# Revit family: Maxlogic Panneau de contrôle d'extinction, 4 zone de détection, 1 zone d'extinction
name_source: partatom
category: Fire Alarm Devices
units: mm (PartAtom-declared; Revit-internal decimal feet)

## family parameters
Cut with Voids When Loaded = No
Host = Face
Maintain Annotation Orientation = Yes
OmniClass Number = 23.85.30.21
OmniClass Title = Environmental Detection/Registration
Part Type = Normal
Room Calculation Point = No
Round Connector Dimension = Use Diameter
Shared = No

## types (1)
- Panneau de Contrôle d'Extinction, 4 zone de détection, 1 sortie zone d'extinction
    Adresse ligne 1 = Şerifali Mahallesi Kutup Sokak No:27/1-2-4 Ümraniye TR-34775 İSTANBUL
    Alimentation d'externe = 220 V AC
    Batterie = 2 X (12V DC 7 Ah )
    Code de  Performance = EN 54-2, EN 54-4
    Code de Produit = ML-322
    Cost = 0 $
    Couleur = Blanc
    Default Elevation = 0 mm  [stored 0 ft]
    Description = Panneau de Contrôle d'Extinction, 4 zone de détection, 1 sortie zone d'extinction
    Deuxime Matèriel = Plastique Blanche ABS
    Durée de la garantie Travail = 2
    Durée de la garantie réservé = 2
    Hauteur Nominale = 300 mm
    Largeur Nominale = 100 mm
    Longeur Nominale = 400 mm
    Manuel d'installation = https://mavilielektronik.com
    Manufacturer = Mavili Elektronik Ticaret A.Ş.
    Matériel Principe = Mètale Grise
    Model = Maxlogic
    Numèro de Fax = (+)90 216 466 45 10
    Poids = 3900 gr
    Surface de Montage = Montage  à Mur
    Tempèrature de Fonctionnement = (-5°C) - (+40°C)
    URL = https://www.mavili.com.tr
    Unité de durée de garantie = Ans

note: [stored X ft] marks values corroborated as IEEE doubles in the binary element streams (Revit-internal decimal feet)

## geometry (parser evidence)
native form markers: Sweep x2
no freeform markers — native parametric forms only
